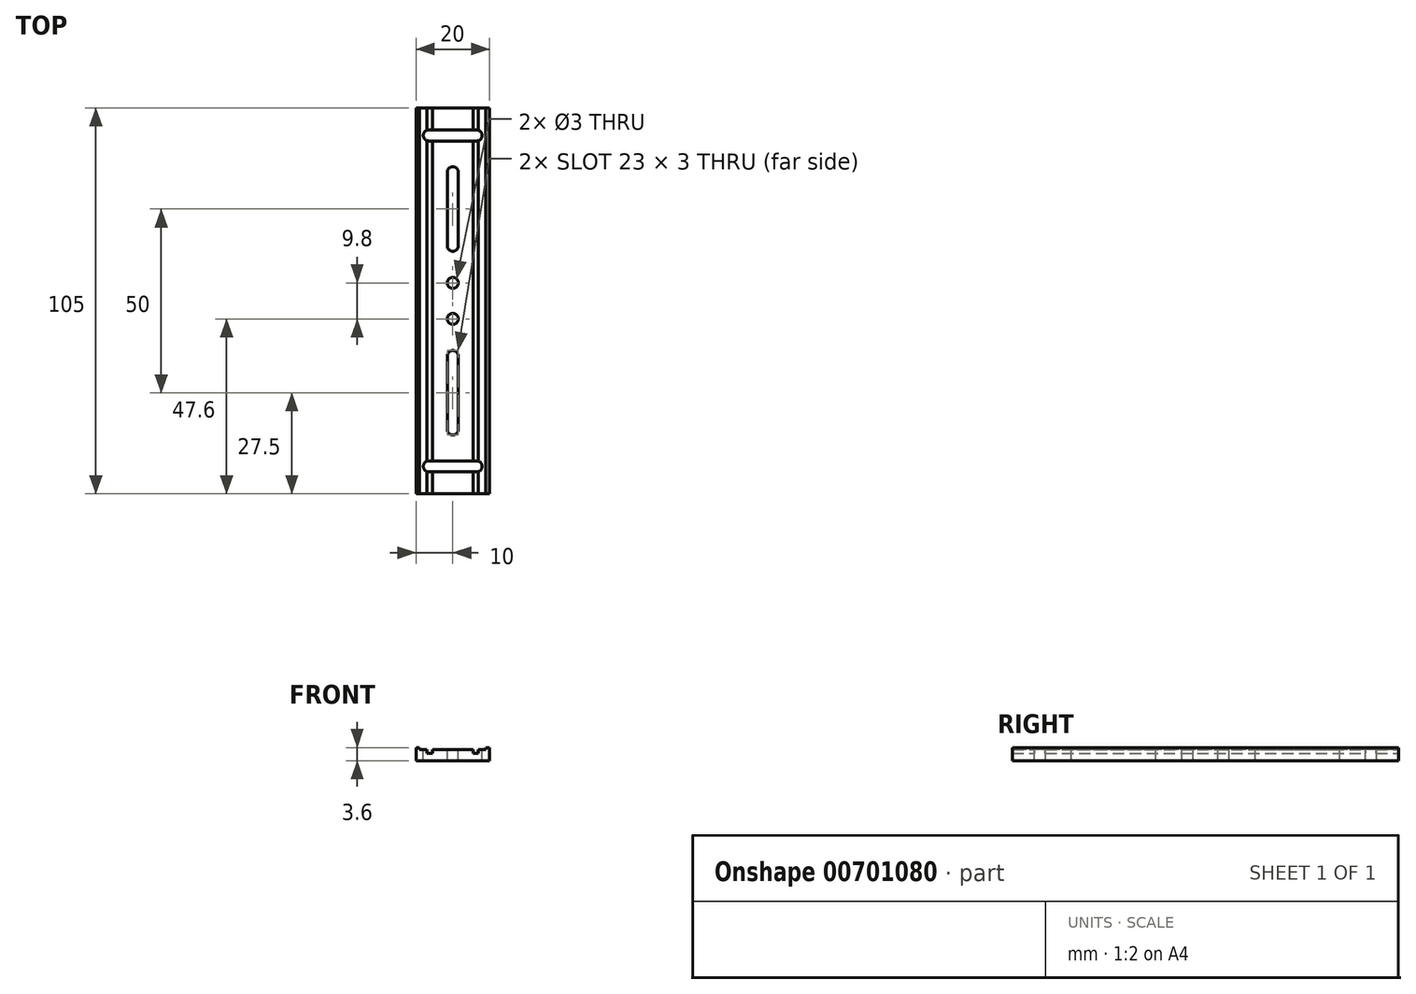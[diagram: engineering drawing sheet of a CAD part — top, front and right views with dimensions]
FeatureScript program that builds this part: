
annotation { "Feature Type Name" : "Feature", "Feature Type Description" : "" }
export const myFeature = defineFeature(function(context is Context, id is Id, definition is map)
    precondition{}
    {
        {
            var Q0;
            Q0=qCreatedBy(makeId("Top.planeOp"),FACE);
            var sketch = newSketch(context, id + "F0", { "sketchPlane" : qUnion([Q0])});
            skLineSegment(sketch, "E0.bottom", {"start": v(0, 0) * mm, "end": v(20, 0) * mm});
            skLineSegment(sketch, "E0.top", {"start": v(0, 105) * mm, "end": v(20, 105) * mm});
            skLineSegment(sketch, "E0.left", {"start": v(0, 0) * mm, "end": v(0, 105) * mm});
            skLineSegment(sketch, "E0.right", {"start": v(20, 0) * mm, "end": v(20, 105) * mm});
            skSolve(sketch);
        }
        {
            var Q0;
            Q0 = qSketchRegion(id + "F0", true);
            extrude(context, id + "F1", {"entities" : qUnion([Q0]), "depth" : 3.1 * mm, "offsetDistance" : 25 * mm});
        }
        {
            var Q0;
            Q0=makeQuery(id+"F1.opExtrude","CAP_FACE",FACE,{"disambiguationData":[OSD([sQuery(id+"F0.wireOp",EDGE,"E0.bottom"),sQuery(id+"F0.wireOp",EDGE,"E0.top"),sQuery(id+"F0.wireOp",EDGE,"E0.left"),sQuery(id+"F0.wireOp",EDGE,"E0.right")])],"isStart":false});
            var sketch = newSketch(context, id + "F2", { "sketchPlane" : qUnion([Q0])});
            skLineSegment(sketch, "E1.bottom", {"start": v(20, 105) * mm, "end": v(19, 105) * mm});
            skLineSegment(sketch, "E1.top", {"start": v(20, 0) * mm, "end": v(19, 0) * mm});
            skLineSegment(sketch, "E1.left", {"start": v(20, 105) * mm, "end": v(20, 0) * mm});
            skLineSegment(sketch, "E1.right", {"start": v(19, 105) * mm, "end": v(19, 0) * mm});
            skLineSegment(sketch, "E2.bottom", {"start": v(0, 105) * mm, "end": v(1, 105) * mm});
            skLineSegment(sketch, "E2.top", {"start": v(0, 0) * mm, "end": v(1, 0) * mm});
            skLineSegment(sketch, "E2.left", {"start": v(0, 105) * mm, "end": v(0, 0) * mm});
            skLineSegment(sketch, "E2.right", {"start": v(1, 105) * mm, "end": v(1, 0) * mm});
            skSolve(sketch);
        }
        {
            var Q0;
            Q0 = qSketchRegion(id + "F2", true);
            extrude(context, id + "F3", {"entities" : qUnion([Q0]), "operationType" : NewBodyOperationType.ADD, "depth" : 0.5 * mm, "offsetDistance" : 25 * mm});
        }
        {
            var Q0;
            Q0=makeQuery(id+"F1.opExtrude","CAP_FACE",FACE,{"disambiguationData":[OSD([sQuery(id+"F0.wireOp",EDGE,"E0.bottom"),sQuery(id+"F0.wireOp",EDGE,"E0.top"),sQuery(id+"F0.wireOp",EDGE,"E0.left"),sQuery(id+"F0.wireOp",EDGE,"E0.right")])],"isStart":false});
            var sketch = newSketch(context, id + "F4", { "sketchPlane" : qUnion([Q0])});
            skLineSegment(sketch, "E3", {"start": v(20, 0) * mm, "end": v(0, 0) * mm});
            skArc(sketch, "E4", {"start": v(3.5, 9) * mm, "mid": v(2, 7.5) * mm, "end": v(3.5, 6) * mm});
            skArc(sketch, "E5", {"start": v(16.5, 6) * mm, "mid": v(18, 7.5) * mm, "end": v(16.5, 9) * mm});
            skLineSegment(sketch, "E6", {"start": v(3.5, 6) * mm, "end": v(16.5, 6) * mm});
            skLineSegment(sketch, "E7", {"start": v(3.5, 9) * mm, "end": v(16.5, 9) * mm});
            skArc(sketch, "E8", {"start": v(8.5, 17.5) * mm, "mid": v(10, 16) * mm, "end": v(11.5, 17.5) * mm});
            skArc(sketch, "E9", {"start": v(11.5, 37.5) * mm, "mid": v(10, 39) * mm, "end": v(8.5, 37.5) * mm});
            skLineSegment(sketch, "E10", {"start": v(11.5, 17.5) * mm, "end": v(11.5, 37.5) * mm});
            skLineSegment(sketch, "E11", {"start": v(8.5, 17.5) * mm, "end": v(8.5, 37.5) * mm});
            skCircle(sketch, "E12", {"center": v(10, 47.6) * mm, "radius": 1.5 * mm});
            skArc(sketch, "E13", {"start": v(3.5, 99) * mm, "mid": v(2, 97.5) * mm, "end": v(3.5, 96) * mm});
            skArc(sketch, "E14", {"start": v(16.5, 96) * mm, "mid": v(18, 97.5) * mm, "end": v(16.5, 99) * mm});
            skLineSegment(sketch, "E15", {"start": v(3.5, 96) * mm, "end": v(16.5, 96) * mm});
            skLineSegment(sketch, "E16", {"start": v(3.5, 99) * mm, "end": v(16.5, 99) * mm});
            skArc(sketch, "E17", {"start": v(11.5, 87.5) * mm, "mid": v(10, 89) * mm, "end": v(8.5, 87.5) * mm});
            skArc(sketch, "E18", {"start": v(8.5, 67.5) * mm, "mid": v(10, 66) * mm, "end": v(11.5, 67.5) * mm});
            skLineSegment(sketch, "E19", {"start": v(8.5, 67.5) * mm, "end": v(8.5, 87.5) * mm});
            skLineSegment(sketch, "E20", {"start": v(11.5, 67.5) * mm, "end": v(11.5, 87.5) * mm});
            skCircle(sketch, "E21", {"center": v(10, 57.4) * mm, "radius": 1.5 * mm});
            skPoint(sketch, "E22.orphan", {"position": v(10, 7.5) * mm});
            skPoint(sketch, "E23.end.orphan", {"position": v(10, 6) * mm});
            skPoint(sketch, "E23.start.orphan", {"position": v(10, 0) * mm});
            skPoint(sketch, "E24.orphan", {"position": v(10, 9) * mm});
            skPoint(sketch, "E25.orphan", {"position": v(10, 16) * mm});
            skPoint(sketch, "E26.orphan", {"position": v(10, 39) * mm});
            skPoint(sketch, "E27.trimOffspring.start.orphan", {"position": v(10, 46.1) * mm});
            skPoint(sketch, "E28.end.orphan", {"position": v(10, 58.9) * mm});
            skPoint(sketch, "E29.start.orphan", {"position": v(10, 66) * mm});
            skPoint(sketch, "E30.start.orphan", {"position": v(10, 96) * mm});
            skPoint(sketch, "E31.orphan", {"position": v(10, 89) * mm});
            skPoint(sketch, "E32.orphan", {"position": v(10, 97.5) * mm});
            skPoint(sketch, "E33.trimOffspring.end.orphan", {"position": v(10, 105) * mm});
            skPoint(sketch, "E33.trimOffspring.start.orphan", {"position": v(10, 99) * mm});
            skSolve(sketch);
        }
        {
            var Q0;
            Q0 = qSketchRegion(id + "F4", true);
            extrude(context, id + "F5", {"entities" : qUnion([Q0]), "operationType" : NewBodyOperationType.REMOVE, "endBound" : BoundingType.THROUGH_ALL, "oppositeDirection" : true, "depth" : 25 * mm, "offsetDistance" : 25 * mm});
        }
        {
            var Q0;
            Q0=makeQuery(id+"F1.opExtrude","CAP_FACE",FACE,{"disambiguationData":[OSD([sQuery(id+"F0.wireOp",EDGE,"E0.bottom"),sQuery(id+"F0.wireOp",EDGE,"E0.top"),sQuery(id+"F0.wireOp",EDGE,"E0.left"),sQuery(id+"F0.wireOp",EDGE,"E0.right")])],"isStart":false});
            var sketch = newSketch(context, id + "F6", { "sketchPlane" : qUnion([Q0])});
            skLineSegment(sketch, "E34", {"start": v(0, 0) * mm, "end": v(3, 0) * mm});
            skLineSegment(sketch, "E35", {"start": v(20, 0) * mm, "end": v(17, 0) * mm});
            skLineSegment(sketch, "E36.bottom", {"start": v(3, 0) * mm, "end": v(4.5, 0) * mm});
            skLineSegment(sketch, "E36.top", {"start": v(3, 105) * mm, "end": v(4.5, 105) * mm});
            skLineSegment(sketch, "E36.left", {"start": v(3, 0) * mm, "end": v(3, 105) * mm});
            skLineSegment(sketch, "E36.right", {"start": v(4.5, 0) * mm, "end": v(4.5, 105) * mm});
            skLineSegment(sketch, "E37.bottom", {"start": v(17, 0) * mm, "end": v(15.5, 0) * mm});
            skLineSegment(sketch, "E37.top", {"start": v(17, 105) * mm, "end": v(15.5, 105) * mm});
            skLineSegment(sketch, "E37.left", {"start": v(17, 0) * mm, "end": v(17, 105) * mm});
            skLineSegment(sketch, "E37.right", {"start": v(15.5, 0) * mm, "end": v(15.5, 105) * mm});
            skSolve(sketch);
        }
        {
            var Q0;
            Q0 = qSketchRegion(id + "F6", true);
            extrude(context, id + "F7", {"entities" : qUnion([Q0]), "operationType" : NewBodyOperationType.REMOVE, "oppositeDirection" : true, "depth" : 1 * mm, "offsetDistance" : 25 * mm});
        }
    });
